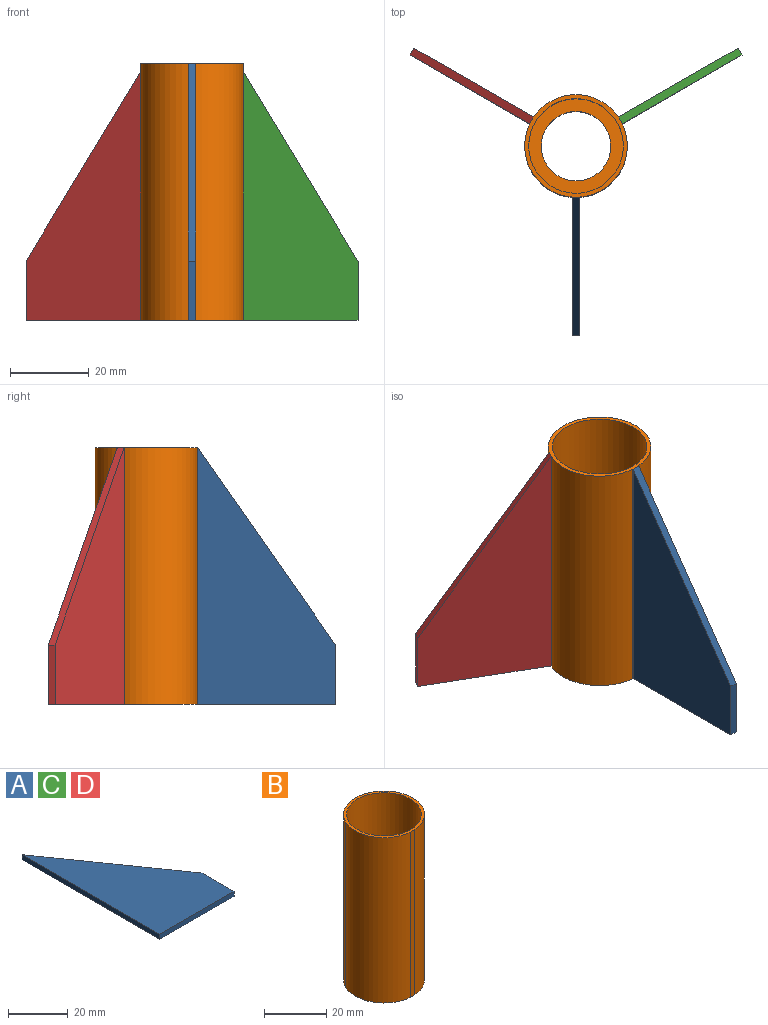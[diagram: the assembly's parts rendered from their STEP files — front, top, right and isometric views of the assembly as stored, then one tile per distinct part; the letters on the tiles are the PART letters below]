
ASSEMBLY  parts=4 mates=1
PART A: 6 faces, bbox 35x65x2 mm
  f0: plane 65x2mm, normal (-1,0,0), area 130mm2, adj f1,f3,f4,f5
  f1: plane 35.01x2mm, normal (0,-1,0), area 70mm2, adj f0,f2,f4,f5
  f2: plane 15x2mm, normal (1,0,0), area 30mm2, adj f1,f3,f4,f5
  f3: plane 50x35.01mm, normal (0.82,0.57,0), area 122.1mm2, adj f0,f2,f4,f5
  f4: plane 65x35.01mm, normal (0,0,1), area 1400.4mm2, adj f0,f1,f2,f3
  f5: plane 65x35.01mm, normal (0,0,-1), area 1400.4mm2, adj f0,f1,f2,f3
PART B: 17 faces, bbox 26x26x65 mm
  f0: cylinder r=12mm len=40mm, axis (0,0,-1), area 3015.9mm2, adj f4,f16
  f1: cylinder r=13mm len=65mm, axis (0,0,-1), area 1639.6mm2, adj f4,f5,f6,f13
  f2: cylinder r=13mm len=65mm, axis (0,0,-1), area 1639.6mm2, adj f4,f5,f10,f14
  f3: cylinder r=13mm len=65mm, axis (0,0,-1), area 1639.6mm2, adj f4,f5,f8,f11
  f4: plane 26x26mm, normal (0,0,1), area 78.6mm2, adj f0,f1,f2,f3,f6,f7,f8,f9
  f5: plane 26x26mm, normal (0,0,-1), area 287.7mm2, adj f1,f2,f3,f6,f7,f8,f9,f10
  f6: plane 65x0.03mm, normal (0.5,0.87,0), area 2.5mm2, adj f1,f4,f5,f7
  f7: plane 65x1.73mm, normal (-0.87,0.5,0), area 130mm2, adj f4,f5,f6,f8
  f8: plane 65x0.03mm, normal (-0.5,-0.87,0), area 2.5mm2, adj f3,f4,f5,f7
  f9: plane 65x2mm, normal (0,-1,0), area 130mm2, adj f4,f5,f10,f11
  f10: plane 65x0.04mm, normal (1,0,0), area 2.5mm2, adj f2,f4,f5,f9
  f11: plane 65x0.04mm, normal (-1,0,0), area 2.5mm2, adj f3,f4,f5,f9
  f12: plane 65x1.73mm, normal (0.87,0.5,0), area 130mm2, adj f4,f5,f13,f14
  f13: plane 65x0.03mm, normal (-0.5,0.87,0), area 2.5mm2, adj f1,f4,f5,f12
  f14: plane 65x0.03mm, normal (0.5,-0.87,0), area 2.5mm2, adj f2,f4,f5,f12
  f15: cylinder r=8.8mm len=25mm, axis (0,0,-1), area 1382.3mm2, adj f5,f16
  f16: plane 24x24mm, normal (0,0,1), area 209.1mm2, adj f0,f15
PART C: same geometry as A
PART D: same geometry as A
PLACE A rot(axis=(0.58,-0.58,-0.58),120deg) t=(1,-13,15)mm
PLACE B at identity
PLACE C rot(axis=(0.94,0.25,0.25),93.8deg) t=(10.76,7.37,15)mm
PLACE D rot(axis=(0.19,0.69,0.69),158.9deg) t=(-11.76,5.63,15)mm
MATE fastened A.f0 <-> B.f9  axis (0,1,0) through (0,-13,32.5)mm
